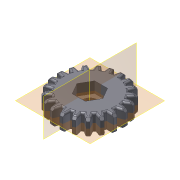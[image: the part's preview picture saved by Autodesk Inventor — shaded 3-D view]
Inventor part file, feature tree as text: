
AUTODESK INVENTOR PART (.ipt)
format: ipt  version: 2015 SP2 (Build 190223200, 223)  size: 908,800 bytes
history: native  units: mm (DEFAULTED — no unit token found)
features: sketch x5, plane x4, extrude x3, other x3, fillet x2, revolve x1, mirror x1, chamfer x1
ambient origin geometry x8: Origin, YZ Plane, XZ Plane, XY Plane, X Axis, Y Axis, Z Axis, Center Point
bodies: Body1 (feature_tree), Body2 (feature_tree)
feature tree (20):
  extrude  "Extrusion1"  Depth=10.0mm TaperAngle=0.0deg
  plane  "Work Plane2"
  plane  "Work Plane8"
  plane  "Work Plane9"
  other  "Engranaje recto"
  extrude  "Extrusión2"  Depth=10.0mm TaperAngle=0.0deg
  extrude  "Extrusión3"  Depth=1.495997mm TaperAngle=0.0deg
  revolve  "Revolución1"  [1 undecoded]
  plane  "Plano de trabajo11"
  mirror  "Simetría1"
  fillet  "Empalme1"  Radius=37.0mm
  fillet  "Empalme2"  Radius=37.0mm
  chamfer  "Chaflán1"  [1 undecoded]
  sketch  "Sketch1"  dims[d0=40.237457mm d1=10.0mm d2=0.0mm]
  sketch  "Sketch2"  dims[d3=37.0mm d4=10.0mm d5=0.0mm]
  other  "Srf1"
  sketch  "Boceto3"  dims[d16=37.0mm d17=0.0mm d34=1.495997mm]
  sketch  "Boceto4"  dims[d39=0.0mm d41=0.0mm d43=37.0mm d46=37.0mm d47=0.0mm d48=0.0mm]
  sketch  "Boceto5"  dims[d49=8.55mm d50=10.0mm d51=0.0mm d52=13.3mm d53=6.5mm d54=0.0mm d55=0.5mm d56=0.5mm d57=2.0mm d58=2.0mm d59=90.0deg d60=1.0mm d61=1.0mm d62=1.0mm d63=2.0mm d64=45.0deg]
  other  "Diámetro de separación"
note: 2 required parameter values undecoded (feature->parameter linkage not recoverable at this tier; creation-order binding heuristic only, values carry confidence <= 0.55)